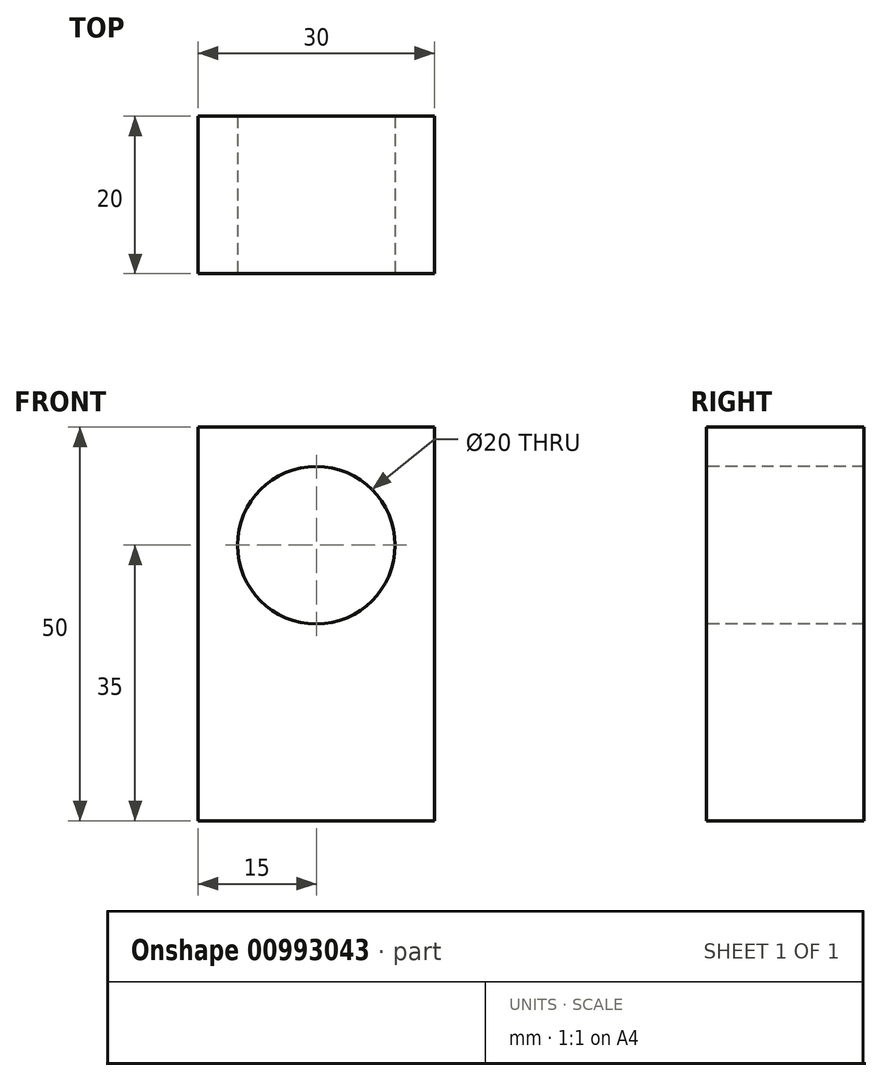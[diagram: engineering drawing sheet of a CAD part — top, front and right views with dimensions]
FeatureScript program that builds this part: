
annotation { "Feature Type Name" : "Feature", "Feature Type Description" : "" }
export const myFeature = defineFeature(function(context is Context, id is Id, definition is map)
    precondition{}
    {
        {
            var Q0;
            Q0=qCreatedBy(makeId("Top.planeOp"),FACE);
            var sketch = newSketch(context, id + "F0", { "sketchPlane" : qUnion([Q0])});
            skLineSegment(sketch, "E0.bottom", {"start": v(15, -10) * mm, "end": v(-15, -10) * mm});
            skLineSegment(sketch, "E0.top", {"start": v(15, 10) * mm, "end": v(-15, 10) * mm});
            skLineSegment(sketch, "E0.left", {"start": v(15, -10) * mm, "end": v(15, 10) * mm});
            skLineSegment(sketch, "E0.right", {"start": v(-15, -10) * mm, "end": v(-15, 10) * mm});
            skPoint(sketch, "E0.middle", {"position": v(0, 0) * mm});
            skSolve(sketch);
        }
        {
            var Q0;
            Q0=makeQuery(id+"F0.imprint","IMPRINT",FACE,{"disambiguationData":[TD([[makeQuery(id+"F0.imprint","IMPRINT",EDGE,{"derivedFrom":sQuery(id+"F0.wireOp",EDGE,"E0.bottom")}),-1.0]])]});
            extrude(context, id + "F1", {"entities" : qUnion([Q0]), "depth" : 50 * mm, "offsetDistance" : 25 * mm});
        }
        {
            var Q0;
            Q0=makeQuery(id+"F1.opExtrude","SWEPT_FACE",FACE,{"disambiguationData":[OSD([sQuery(id+"F0.wireOp",EDGE,"E0.bottom")])]});
            var sketch = newSketch(context, id + "F2", { "sketchPlane" : qUnion([Q0])});
            skPoint(sketch, "E1", {"position": v(0, 35) * mm});
            skPoint(sketch, "E1.positionSnap0", {"position": v(0, 50) * mm});
            skCircle(sketch, "E2", {"center": v(0, 35) * mm, "radius": 10 * mm});
            skSolve(sketch);
        }
        {
            var Q0;
            Q0=makeQuery(id+"F2.imprint","IMPRINT",FACE,{"disambiguationData":[TD([[makeQuery(id+"F2.imprint","IMPRINT",EDGE,{"derivedFrom":sQuery(id+"F2.wireOp",EDGE,"E2")}),1.0]])]});
            extrude(context, id + "F3", {"entities" : qUnion([Q0]), "operationType" : NewBodyOperationType.REMOVE, "oppositeDirection" : true, "depth" : 25 * mm, "offsetDistance" : 25 * mm});
        }
    });
